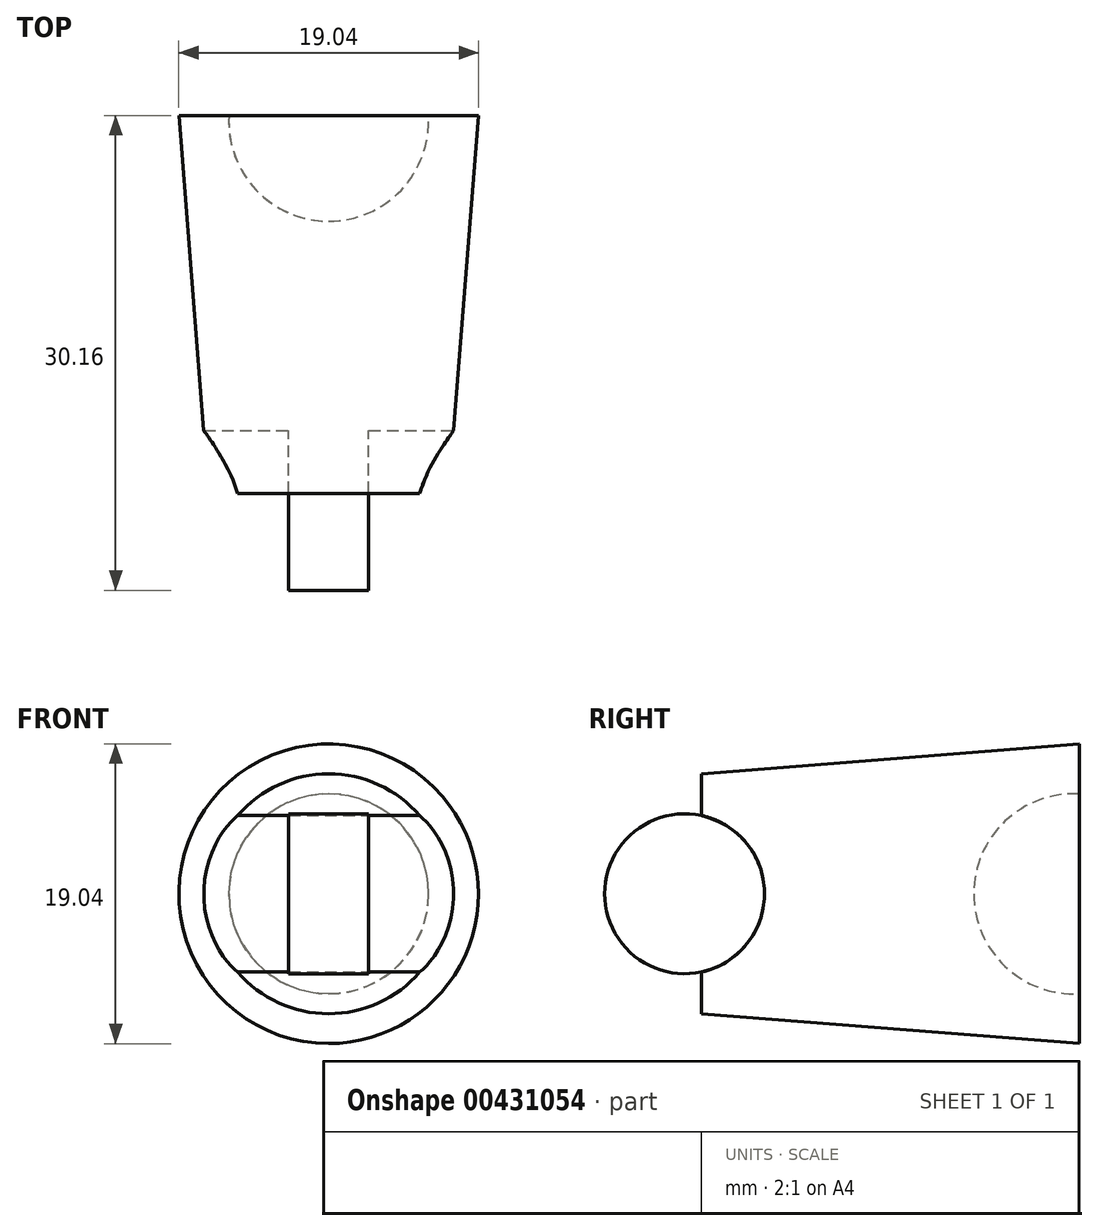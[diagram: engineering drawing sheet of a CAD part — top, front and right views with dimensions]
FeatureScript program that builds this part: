
annotation { "Feature Type Name" : "Feature", "Feature Type Description" : "" }
export const myFeature = defineFeature(function(context is Context, id is Id, definition is map)
    precondition{}
    {
        {
            var Q0;
            Q0=qCreatedBy(makeId("Top.planeOp"),FACE);
            var sketch = newSketch(context, id + "F0", { "sketchPlane" : qUnion([Q0])});
            skCircle(sketch, "E0", {"center": v(0, 10.32) * mm, "radius": 6.35 * mm});
            skLineSegment(sketch, "E1", {"start": v(6.34, 10.68) * mm, "end": v(9.52, 10.68) * mm});
            skLineSegment(sketch, "E2", {"start": v(9.52, 10.68) * mm, "end": v(7.62, -13.32) * mm});
            skLineSegment(sketch, "E3", {"start": v(7.62, -13.32) * mm, "end": v(0, -13.32) * mm});
            skLineSegment(sketch, "E4", {"start": v(0, -13.32) * mm, "end": v(0, 3.97) * mm});
            skSolve(sketch);
        }
        {
            var Q0;
            {var subQ0=sQuery(id+"F0.wireOp",EDGE,"E1");Q0=makeQuery(id+"F0.imprint","IMPRINT",FACE,{"disambiguationData":[TD([[makeQuery(id+"F0.imprint","IMPRINT",EDGE,{"derivedFrom":subQ0}),-1.0]])]});}
            var Q1;
            Q1=sQuery(id+"F0.wireOp",EDGE,"E4");
            revolve(context, id + "F1", {"entities" : qUnion([Q0]), "axis" : qUnion([Q1]), "revolveType" : RevolveType.FULL});
        }
        {
            var Q0;
            Q0=qCreatedBy(makeId("Right.planeOp"),FACE);
            var sketch = newSketch(context, id + "F2", { "sketchPlane" : qUnion([Q0])});
            skCircle(sketch, "E5", {"center": v(-14.4, 0) * mm, "radius": 5.08 * mm});
            skSolve(sketch);
        }
        {
            var Q0;
            Q0=makeQuery(id+"F2.imprint","IMPRINT",FACE,{"disambiguationData":[TD([[makeQuery(id+"F2.imprint","IMPRINT",EDGE,{"derivedFrom":sQuery(id+"F2.wireOp",EDGE,"E5")}),1.0]])]});
            extrude(context, id + "F3", {"entities" : qUnion([Q0]), "operationType" : NewBodyOperationType.REMOVE, "endBound" : BoundingType.SYMMETRIC, "oppositeDirection" : true, "depth" : 50.8 * mm});
        }
        {
            var Q0;
            Q0=makeQuery(id+"F2.imprint","IMPRINT",FACE,{"disambiguationData":[TD([[makeQuery(id+"F2.imprint","IMPRINT",EDGE,{"derivedFrom":sQuery(id+"F2.wireOp",EDGE,"E5")}),1.0]])]});
            var Q1;
            Q1=sQuery(id+"F2.wireOp",EDGE,"E5");
            extrude(context, id + "F4", {"entities" : qUnion([Q0]), "operationType" : NewBodyOperationType.ADD, "surfaceEntities" : qUnion([Q1]), "endBound" : BoundingType.SYMMETRIC, "depth" : 5.08 * mm});
        }
    });
